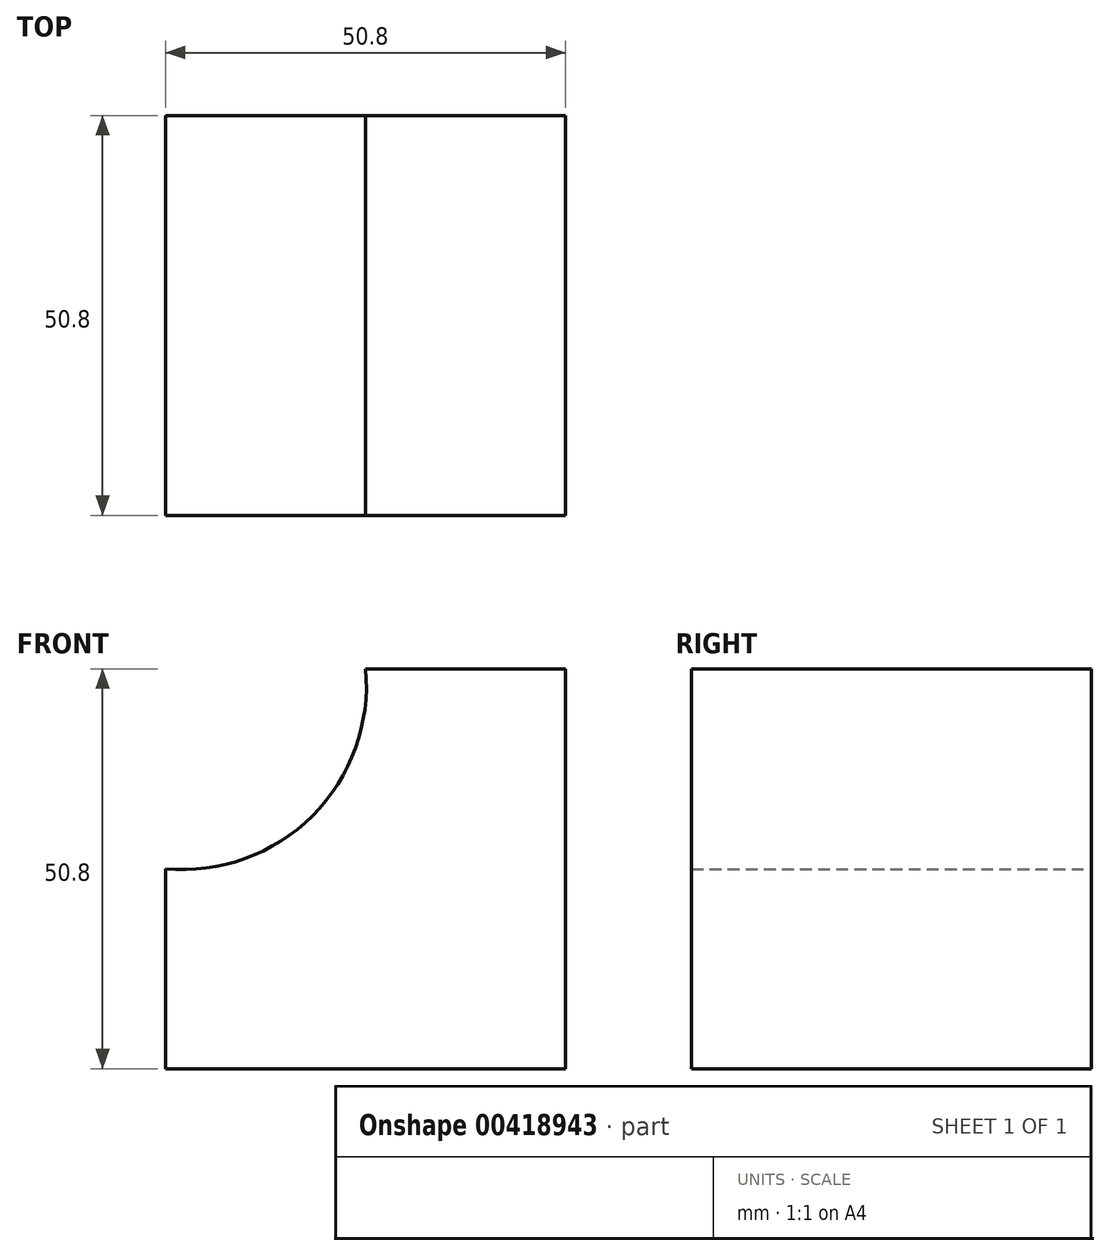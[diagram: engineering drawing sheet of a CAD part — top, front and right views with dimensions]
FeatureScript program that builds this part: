
annotation { "Feature Type Name" : "Feature", "Feature Type Description" : "" }
export const myFeature = defineFeature(function(context is Context, id is Id, definition is map)
    precondition{}
    {
        {
            var Q0;
            Q0=qCreatedBy(makeId("Front.planeOp"),FACE);
            var sketch = newSketch(context, id + "F0", { "sketchPlane" : qUnion([Q0])});
            skLineSegment(sketch, "E0", {"start": v(-50.8, 0) * mm, "end": v(0, 0) * mm});
            skLineSegment(sketch, "E1", {"start": v(0, 0) * mm, "end": v(0, 50.8) * mm});
            skLineSegment(sketch, "E2", {"start": v(0, 50.8) * mm, "end": v(-25.4, 50.8) * mm});
            skLineSegment(sketch, "E3", {"start": v(-50.8, 0) * mm, "end": v(-50.8, 25.4) * mm});
            skArc(sketch, "E4", {"start": v(-50.8, 25.4) * mm, "mid": v(-32.14, 32.14) * mm, "end": v(-25.4, 50.8) * mm});
            skSolve(sketch);
        }
        {
            var Q0;
            Q0 = qSketchRegion(id + "F0", true);
            extrude(context, id + "F1", {"entities" : qUnion([Q0]), "depth" : 50.8 * mm});
        }
    });
